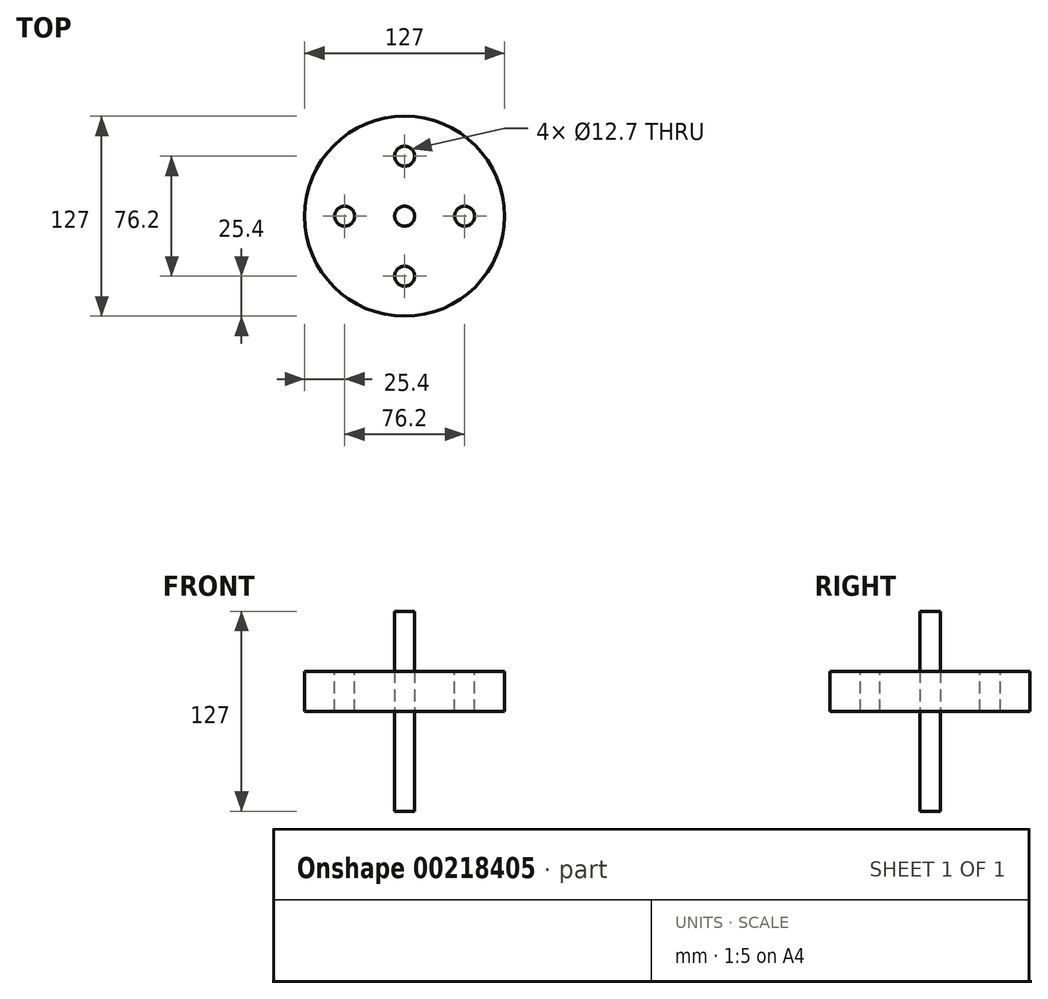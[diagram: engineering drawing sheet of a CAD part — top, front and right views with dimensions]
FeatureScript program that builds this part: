
annotation { "Feature Type Name" : "Feature", "Feature Type Description" : "" }
export const myFeature = defineFeature(function(context is Context, id is Id, definition is map)
    precondition{}
    {
        {
            var Q0;
            Q0=qCreatedBy(makeId("Top.planeOp"),FACE);
            var sketch = newSketch(context, id + "F0", { "sketchPlane" : qUnion([Q0])});
            skCircle(sketch, "E0", {"center": v(0, 0) * mm, "radius": 63.5 * mm});
            skSolve(sketch);
        }
        {
            var Q0;
            Q0 = qSketchRegion(id + "F0", true);
            extrude(context, id + "F1", {"entities" : qUnion([Q0]), "depth" : 25.4 * mm});
        }
        {
            var Q0;
            Q0=makeQuery(id+"F1.opExtrude","CAP_FACE",FACE,{"disambiguationData":[OSD([sQuery(id+"F0.wireOp",EDGE,"E0")])],"isStart":false});
            var sketch = newSketch(context, id + "F2", { "sketchPlane" : qUnion([Q0])});
            skCircle(sketch, "E1", {"center": v(-38.1, 0) * mm, "radius": 6.35 * mm});
            skCircle(sketch, "E2.1.0", {"center": v(0, -38.1) * mm, "radius": 6.35 * mm});
            skCircle(sketch, "E2.2.0", {"center": v(38.1, 0) * mm, "radius": 6.35 * mm});
            skCircle(sketch, "E2.3.0", {"center": v(0, 38.1) * mm, "radius": 6.35 * mm});
            skPoint(sketch, "E2.center", {"position": v(0, 0) * mm});
            skSolve(sketch);
        }
        {
            var Q0;
            Q0 = qSketchRegion(id + "F2", true);
            extrude(context, id + "F3", {"entities" : qUnion([Q0]), "operationType" : NewBodyOperationType.REMOVE, "endBound" : BoundingType.THROUGH_ALL, "oppositeDirection" : true, "depth" : 25.4 * mm});
        }
        {
            var Q0;
            Q0=qCreatedBy(makeId("Top.planeOp"),FACE);
            var sketch = newSketch(context, id + "F4", { "sketchPlane" : qUnion([Q0])});
            skCircle(sketch, "E3", {"center": v(0, 0) * mm, "radius": 6.35 * mm});
            skSolve(sketch);
        }
        {
            var Q0;
            Q0 = qSketchRegion(id + "F4", true);
            extrude(context, id + "F5", {"entities" : qUnion([Q0]), "endBound" : BoundingType.SYMMETRIC, "depth" : 127 * mm});
        }
    });
